FCSTD DOCUMENT  (FreeCAD 0.19R16945 (Git))
Label: Panasonic ERJ Footprint
License: All rights reserved
LicenseURL: http://en.wikipedia.org/wiki/All_rights_reserved
objects: Sketcher::SketchObject×1, App::DocumentObjectGroup×1
note: 1 computed .brp shape members not serialized (recipe doc carries the construction recipe); baked Part::Feature solids carry a one-line shape summary decoded from their .brp

FEATURE [Sketcher::SketchObject] Sketch  label="Pads_TH_SMD"
  sketch-geometry (8):
    g0: LineSegment StartX=-0.4 StartY=-0.45 StartZ=0 EndX=-1.05 EndY=-0.45 EndZ=0
    g1: LineSegment StartX=-1.05 StartY=-0.45 StartZ=0 EndX=-1.05 EndY=0.45 EndZ=0
    g2: LineSegment StartX=-1.05 StartY=0.45 StartZ=0 EndX=-0.4 EndY=0.45 EndZ=0
    g3: LineSegment StartX=-0.4 StartY=0.45 StartZ=0 EndX=-0.4 EndY=-0.45 EndZ=0
    g4: LineSegment StartX=0.4 StartY=-0.45 StartZ=0 EndX=1.05 EndY=-0.45 EndZ=0
    g5: LineSegment StartX=1.05 StartY=-0.45 StartZ=0 EndX=1.05 EndY=0.45 EndZ=0
    g6: LineSegment StartX=1.05 StartY=0.45 StartZ=0 EndX=0.4 EndY=0.45 EndZ=0
    g7: LineSegment StartX=0.4 StartY=0.45 StartZ=0 EndX=0.4 EndY=-0.45 EndZ=0
  constraints (21):
    c: Coincident(g0,g1)
    c: Coincident(g1,g2)
    c: Coincident(g2,g3)
    c: Coincident(g3,g0)
    c: Horizontal(g0)
    c: Horizontal(g2)
    c: Vertical(g1)
    c: Coincident(g4,g5)
    c: Coincident(g5,g6)
    c: Coincident(g6,g7)
    c: Coincident(g7,g4)
    c: Horizontal(g4)
    c: Symmetric(g5,g4,g-1)
    c: Symmetric(g2,g0,g-1)
    c: DistanceX(g2,g6) = 0.8
    c: Equal(g2,g6)
    c: Equal(g1,g7)
    c: DistanceY(g1,g1) = 0.9
    c: DistanceX(g1,g5) = 2.1
    c: Symmetric(g0,g4,g-2)
    c: Vertical(g7)
FEATURE [App::DocumentObjectGroup] Group  label="Panasonic_ERJ-3EKF"
  Group = -> [Sketch]
